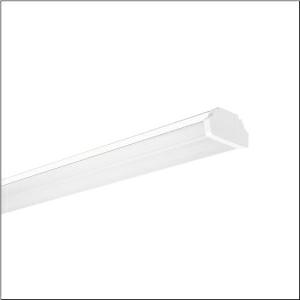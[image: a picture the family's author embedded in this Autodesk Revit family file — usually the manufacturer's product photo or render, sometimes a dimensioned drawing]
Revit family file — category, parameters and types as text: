
# Revit family: dus_r__31_ho_53bd812m1v4120_db1b
name_source: partatom
category: Lighting Fixtures
units: mm (PartAtom-declared; Revit-internal decimal feet)

## family parameters
Cut with Voids When Loaded = No
Host = Face
Light Source = No
Part Type = Normal
Room Calculation Point = No
Round Connector Dimension = Use Diameter
Shared = No

## types (1)
- --- (1 x LED, 12380 lm, 77.3 W, 4000K)
    Apparent Load = 77 VA
    CIE Flux Codes = 47 80 95 92 100
    Color Rendering = 80
    Color Temperature = 4000K
    Default Elevation = 1800 mm
    Description = DUS® 31 HO, luminaire insert, of sheet steel, coil coated, white, length: 1.535mm, width: 81mm, height: 90mm, 5x system unit, system units: 307mm, LED rated luminous flux: 12.380lm, light colour: 840, control gear: ON/OFF Multilumen, control gear: ECG Multilumen, with plug, 3-pole, with phase selection, mains connection: 220..240V, AC, 50/60Hz, rated input power: 77W, through-wiring accessed according to module size, primary optical cover: cover, of PMMA, light emission: direct distribution, primary light characteristic: symmetric, protection rating (complete): IP20, protection rating (LED compartment): IP50, insulation class (complete): insulation class I (protective earthing), certification: CE, ENEC, VDE, UKCA, impact resistance: IK03, permissible ambient temperature for indoor applications: -35..+35°C, corresponds to IFS (International Featured Standards) requirements for safety and quality in the food industry, reducing of maximum allowable ambient temperature of 5°C with ceiling mounting, packaging unit: 1 piece
    Height = 95 mm
    Lamp = 1 x LED
    Lamp Light Flux = 12380 lm
    Lamp Power = 77.3 W
    Lamp count = 1
    Length = 1535 mm
    Luminous efficacy = 160 lm/W
    Manufacturer = Siteco
    ModVariant = No
    Model = 53BD812M1V4120
    Mounting Place = Ceiling
    Mounting Type = Pendant
    Number of Poles = 1
    OnlyDefault = Yes
    Power Factor = 1
    Product Name = DUS® 31 HO
    Product group = luminaire insert
    ProductGroupID = 901
    Protection Class = Protection class I
    Protection Degree = IP 20
    RLX_Detail_Level = 1
    RLX_Emergency_Light_Flux = 0 lm
    RLX_Emergency_Type = 0
    RLX_Emergency_Type_DB = No
    RlxData = <blob elided: 39761 chars, md5=8a3ca9c4>
    Socket = socket
    Standby Power = 0 W
    System Light Flux = 12380 lm
    System Power = 77 W
    Type Comments = factory setting: luminous flux: 100 % | (A | C | E) | 173 mA
    Type Image = l_1003451.jpg
    URL = http://relux.com
    VarID = @adj_140187
    Voltage = 0 V
    Weight = 0.00 kg
    Width = 81 mm

## geometry (parser evidence)
native form markers: Blend x4, Sweep x12
no freeform markers — native parametric forms only
